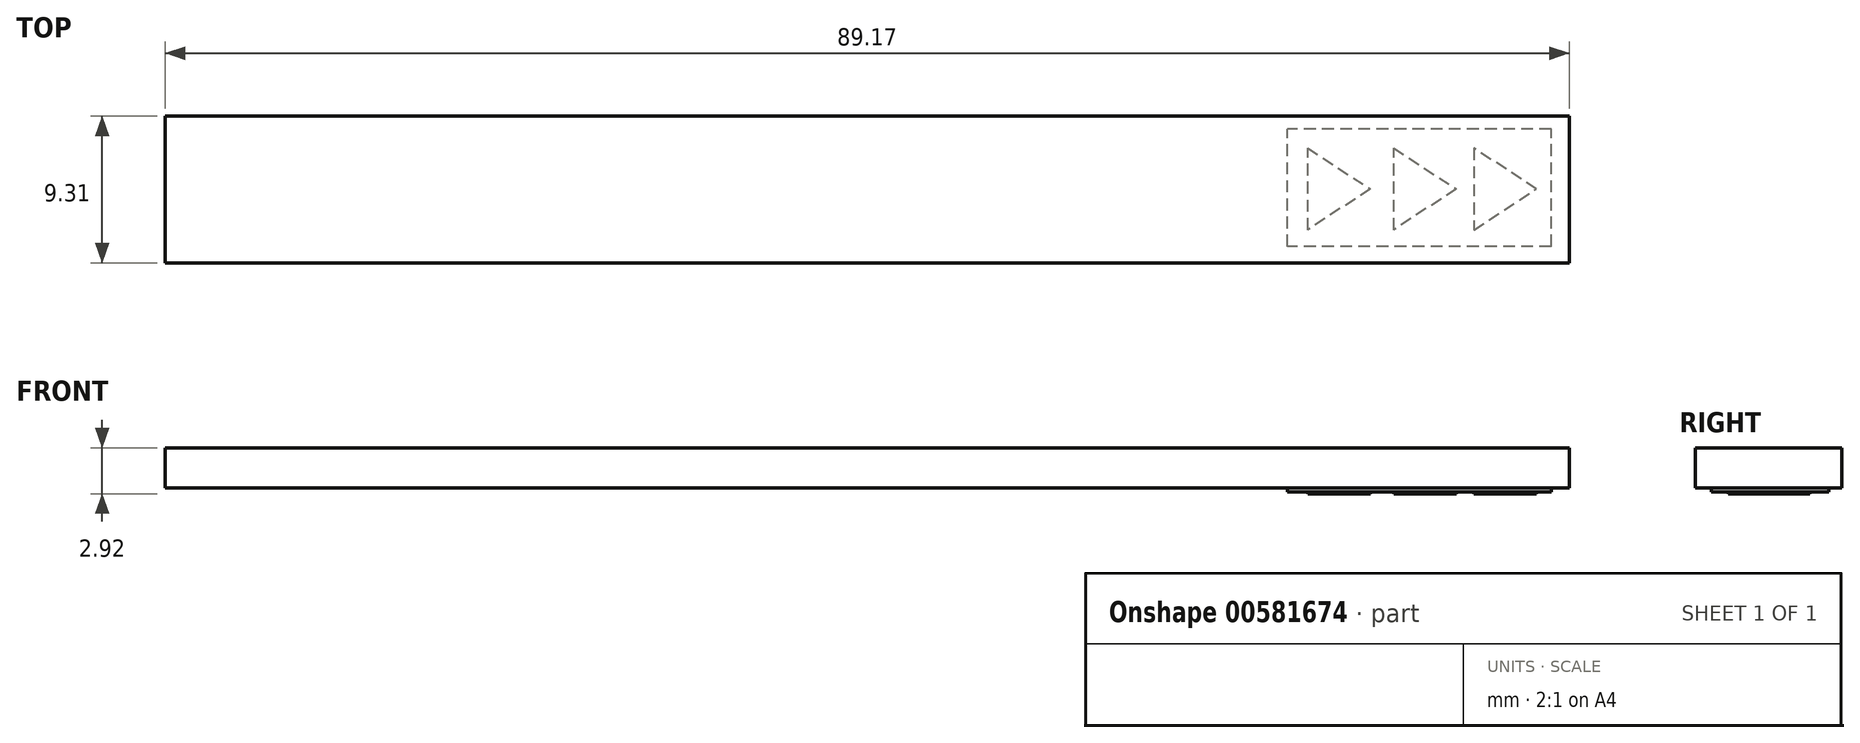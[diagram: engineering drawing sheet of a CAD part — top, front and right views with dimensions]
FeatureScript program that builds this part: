
annotation { "Feature Type Name" : "Feature", "Feature Type Description" : "" }
export const myFeature = defineFeature(function(context is Context, id is Id, definition is map)
    precondition{}
    {
        {
            var Q0;
            Q0=qCreatedBy(makeId("Top.planeOp"),FACE);
            var sketch = newSketch(context, id + "F0", { "sketchPlane" : qUnion([Q0])});
            skLineSegment(sketch, "E0.bottom", {"start": v(-44.36, -21.7) * mm, "end": v(44.8, -21.7) * mm});
            skLineSegment(sketch, "E0.top", {"start": v(-44.36, -12.38) * mm, "end": v(44.8, -12.38) * mm});
            skLineSegment(sketch, "E0.left", {"start": v(-44.36, -21.7) * mm, "end": v(-44.36, -12.38) * mm});
            skLineSegment(sketch, "E0.right", {"start": v(44.8, -21.7) * mm, "end": v(44.8, -12.38) * mm});
            skSolve(sketch);
        }
        {
            var Q0;
            Q0 = qSketchRegion(id + "F0", true);
            extrude(context, id + "F1", {"entities" : qUnion([Q0]), "depth" : 2.54 * mm, "offsetDistance" : 25.4 * mm});
        }
        {
            var Q0;
            Q0=makeQuery(id+"F1.opExtrude","CAP_FACE",FACE,{"disambiguationData":[OSD([sQuery(id+"F0.wireOp",EDGE,"E0.bottom"),sQuery(id+"F0.wireOp",EDGE,"E0.top"),sQuery(id+"F0.wireOp",EDGE,"E0.left"),sQuery(id+"F0.wireOp",EDGE,"E0.right")])],"isStart":true});
            var sketch = newSketch(context, id + "F2", { "sketchPlane" : qUnion([Q0])});
            skLineSegment(sketch, "E1.bottom", {"start": v(43.66, 20.66) * mm, "end": v(26.9, 20.66) * mm});
            skLineSegment(sketch, "E1.top", {"start": v(43.66, 13.21) * mm, "end": v(26.9, 13.21) * mm});
            skLineSegment(sketch, "E1.left", {"start": v(43.66, 20.66) * mm, "end": v(43.66, 13.21) * mm});
            skLineSegment(sketch, "E1.right", {"start": v(26.9, 20.66) * mm, "end": v(26.9, 13.21) * mm});
            skSolve(sketch);
        }
        {
            var Q0;
            Q0 = qSketchRegion(id + "F2", true);
            extrude(context, id + "F3", {"entities" : qUnion([Q0]), "operationType" : NewBodyOperationType.ADD, "depth" : 0.25 * mm, "offsetDistance" : 25.4 * mm});
        }
        {
            var Q0;
            Q0=makeQuery(id+"F3.opExtrude","CAP_FACE",FACE,{"disambiguationData":[OSD([sQuery(id+"F2.wireOp",EDGE,"E1.bottom"),sQuery(id+"F2.wireOp",EDGE,"E1.top"),sQuery(id+"F2.wireOp",EDGE,"E1.left"),sQuery(id+"F2.wireOp",EDGE,"E1.right")])],"isStart":false});
            var sketch = newSketch(context, id + "F4", { "sketchPlane" : qUnion([Q0])});
            skLineSegment(sketch, "E2", {"start": v(28.2, 19.6) * mm, "end": v(28.2, 14.41) * mm});
            skLineSegment(sketch, "E3", {"start": v(28.2, 14.41) * mm, "end": v(32.18, 17) * mm});
            skLineSegment(sketch, "E4", {"start": v(32.18, 17) * mm, "end": v(28.2, 19.6) * mm});
            skLineSegment(sketch, "E5", {"start": v(33.66, 19.6) * mm, "end": v(33.66, 14.41) * mm});
            skLineSegment(sketch, "E6", {"start": v(33.66, 14.41) * mm, "end": v(37.64, 17) * mm});
            skPoint(sketch, "E6.endSnap0", {"position": v(33.66, 17) * mm});
            skLineSegment(sketch, "E7", {"start": v(37.64, 17) * mm, "end": v(33.66, 19.6) * mm});
            skLineSegment(sketch, "E8", {"start": v(38.75, 19.6) * mm, "end": v(42.73, 17) * mm});
            skLineSegment(sketch, "E9", {"start": v(42.73, 17) * mm, "end": v(38.75, 14.41) * mm});
            skLineSegment(sketch, "E10", {"start": v(38.75, 14.41) * mm, "end": v(38.75, 19.6) * mm});
            skSolve(sketch);
        }
        {
            var Q0;
            Q0 = qSketchRegion(id + "F4", true);
            extrude(context, id + "F5", {"entities" : qUnion([Q0]), "operationType" : NewBodyOperationType.ADD, "depth" : 0.13 * mm, "offsetDistance" : 25.4 * mm});
        }
    });
